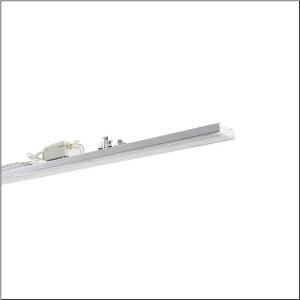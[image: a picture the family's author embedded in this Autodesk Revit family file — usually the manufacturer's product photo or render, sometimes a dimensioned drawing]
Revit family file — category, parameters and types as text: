
# Revit family: licross_r__21_recessed_mo_52tl18vn48xg_e29d
name_source: partatom
category: Lighting Fixtures
units: mm (PartAtom-declared; Revit-internal decimal feet)

## family parameters
Cut with Voids When Loaded = No
Host = Face
Light Source = No
Part Type = Normal
Room Calculation Point = No
Round Connector Dimension = Use Diameter
Shared = No

## types (1)
- --- (1 x LED, 8000 lm, 45.7 W, 4000K)
    Apparent Load = 46 VA
    CIE Flux Codes = 79 95 99 100 100
    Color Rendering = 80
    Color Temperature = 4000K
    Default Elevation = 1800 mm
    Description = Licross® 21 Recessed MO, luminaire insert, of sheet steel, galvanised, coil coated, white, length: 1.500mm, width: 66mm, height: 67mm, LED rated luminous flux: 8.000lm, light colour: 840, control gear: DALI 2, CLO, with plug, 5-pole, with phase selection, mains connection: 220..240V, AC, 50/60Hz, start of lifetime: 46W, end of service life: 54W, halogen-free wiring, primary optical cover: cover, of PMMA, light emission: direct distribution, primary light characteristic: symmetric, protection rating (complete): IP40, insulation class (complete): insulation class I (protective earthing), certification: CE, ENEC, VDE, UKCA, protection symbol: D if used in an environment without relevant dust loads with corresponding accessories, impact resistance: IK06, permissible ambient temperature for indoor applications: -25..+40°C, corresponds to IFS (International Featured Standards) requirements for safety and quality in the food industry, reducing of maximum allowable ambient temperature of 5°C with ceiling mounting, LABS conformity tested according to VDMA 24364:2018-05, packaging unit: 1 piece
    Height = 58 mm
    Lamp = 1 x LED
    Lamp Light Flux = 8000 lm
    Lamp Power = 45.7 W
    Lamp count = 1
    Length = 1500 mm
    Luminous efficacy = 175 lm/W
    Manufacturer = Siteco
    ModVariant = No
    Model = 52TL18VN48XG
    Mounting Place = Ceiling
    Mounting Type = Pendant
    Number of Poles = 1
    OnlyDefault = Yes
    Power Factor = 1
    Product Name = Licross® 21 Recessed MO
    Product group = luminaire insert
    ProductGroupID = 901
    Protection Class = Protection class I
    Protection Degree = IP 40
    RLX_Detail_Level = 1
    RLX_Emergency_Light_Flux = 0 lm
    RLX_Emergency_Type = 0
    RLX_Emergency_Type_DB = No
    RlxData = <blob elided: 24549 chars, md5=0127e5cb>
    Socket = socket
    Standby Power = 0 W
    System Light Flux = 8000 lm
    System Power = 46 W
    Type Comments = factory setting: luminous flux: 100 % | dim-lin: 254 | 307 mA
    Type Image = l_1296930.jpg
    URL = http://relux.com
    VarID = @adj_051473
    Voltage = 0 V
    Weight = 0.00 kg
    Width = 66 mm

## geometry (parser evidence)
native form markers: Blend x4, Sweep x9
no freeform markers — native parametric forms only
